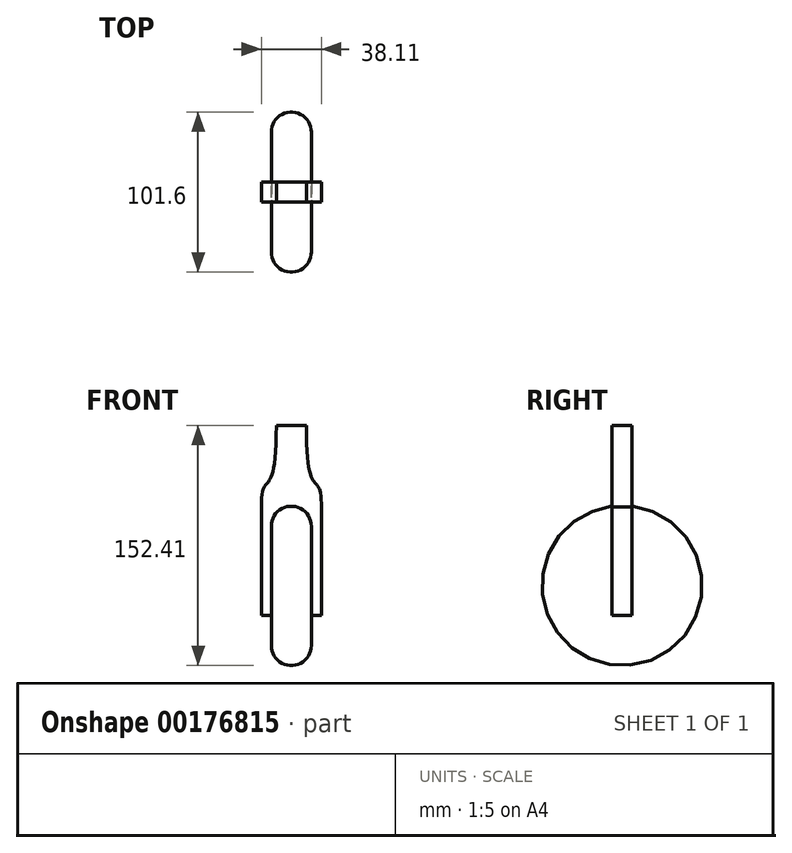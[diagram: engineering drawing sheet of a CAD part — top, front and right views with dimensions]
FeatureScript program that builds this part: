
annotation { "Feature Type Name" : "Feature", "Feature Type Description" : "" }
export const myFeature = defineFeature(function(context is Context, id is Id, definition is map)
    precondition{}
    {
        {
            var Q0;
            Q0=qCreatedBy(makeId("Right.planeOp"),FACE);
            var sketch = newSketch(context, id + "F0", { "sketchPlane" : qUnion([Q0])});
            skCircle(sketch, "E0", {"center": v(0, 0) * mm, "radius": 50.8 * mm});
            skCircle(sketch, "E1", {"center": v(0, 0) * mm, "radius": 6.35 * mm});
            skSolve(sketch);
        }
        {
            var Q0;
            Q0=makeQuery(id+"F0.imprint","IMPRINT",FACE,{"disambiguationData":[TD([[makeQuery(id+"F0.imprint","IMPRINT",EDGE,{"derivedFrom":sQuery(id+"F0.wireOp",EDGE,"E0")}),1.0]])]});
            extrude(context, id + "F1", {"entities" : qUnion([Q0]), "endBound" : BoundingType.SYMMETRIC, "depth" : 25.4 * mm});
        }
        {
            var Q0;
            Q0=makeQuery(id+"F1.opExtrude","CAP_EDGE",EDGE,{"disambiguationData":[OSD([sQuery(id+"F0.wireOp",EDGE,"E0")])],"isStart":false});
            var Q1;
            Q1=makeQuery(id+"F1.opExtrude","CAP_EDGE",EDGE,{"disambiguationData":[OSD([sQuery(id+"F0.wireOp",EDGE,"E0")])],"isStart":true});
            fillet(context, id + "F2", {"entities" : qUnion([Q0, Q1]), "radius" : 12.7 * mm, "tangentPropagation" : true, "allowEdgeOverflow" : false});
        }
        {
            var Q0;
            Q0=qCreatedBy(makeId("Front.planeOp"),FACE);
            var sketch = newSketch(context, id + "F3", { "sketchPlane" : qUnion([Q0])});
            skLineSegment(sketch, "E2.left", {"start": v(19.05, 52.1) * mm, "end": v(19.05, -19.05) * mm});
            skLineSegment(sketch, "E2.right", {"start": v(-19.05, 49.9) * mm, "end": v(-19.05, -19.05) * mm});
            skPoint(sketch, "E2.middle", {"position": v(0, 0) * mm});
            skLineSegment(sketch, "E3", {"start": v(-19.05, 0) * mm, "end": v(-19.05, -19.05) * mm});
            skLineSegment(sketch, "E4", {"start": v(-19.05, -19.05) * mm, "end": v(19.05, -19.05) * mm});
            skLineSegment(sketch, "E5", {"start": v(19.05, -19.05) * mm, "end": v(19.05, 0) * mm});
            skLineSegment(sketch, "E6", {"start": v(-9.52, 101.54) * mm, "end": v(0, 101.54) * mm});
            skLineSegment(sketch, "E7", {"start": v(0, 101.54) * mm, "end": v(9.52, 101.6) * mm});
            skFitSpline(sketch, "E8", {"points": [v(-19.05, 49.9) * mm, v(-9.52, 101.54) * mm], "startDerivative": vector(0, 79.44) * mm, "endDerivative": vector(0, 154.9) * mm});
            skFitSpline(sketch, "E9", {"points": [v(19.05, 49.9) * mm, v(9.52, 101.6) * mm], "startDerivative": vector(0.9, 78.02) * mm, "endDerivative": vector(0, 155.11) * mm});
            skPoint(sketch, "E2.bottom.end.orphan", {"position": v(-19.05, 101.54) * mm});
            skPoint(sketch, "E2.bottom.start.orphan", {"position": v(19.05, 101.67) * mm});
            skSolve(sketch);
        }
        {
            var Q0;
            Q0 = qSketchRegion(id + "F3", true);
            extrude(context, id + "F4", {"entities" : qUnion([Q0]), "operationType" : NewBodyOperationType.ADD, "endBound" : BoundingType.SYMMETRIC, "depth" : 12.7 * mm});
        }
    });
